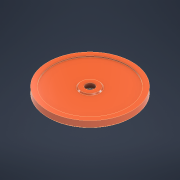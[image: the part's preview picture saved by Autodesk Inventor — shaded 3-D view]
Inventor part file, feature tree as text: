
AUTODESK INVENTOR PART (.ipt)
format: ipt  version: 2022 (Build 260153000, 153)  size: 141,824 bytes
history: native  units: mm
features: chamfer x2, revolve x1, sketch x1
ambient origin geometry x8: Origin, YZ Plane, XZ Plane, XY Plane, X Axis, Y Axis, Z Axis, Center Point
bodies: Solid1 (feature_tree)
feature tree (4):
  revolve  "Revolution1"  [1 undecoded]
  chamfer  "Chamfer1"  Angle=360.0deg  [1 undecoded]
  chamfer  "Chamfer2"  Distance=1.0mm
  sketch  "Sketch1"  dims[d0=8.0mm d3=16.0mm d7=360.0deg d8=1.0mm d9=1.0mm d10=4.0mm d11=78.0mm d12=1.0mm d13=2.0mm d14=45.0deg d15=0.5mm d16=2.0mm d17=45.0deg d18=69.0mm d23=0.25mm d24=2.0mm]
note: 2 required parameter values undecoded (feature->parameter linkage not recoverable at this tier; creation-order binding heuristic only, values carry confidence <= 0.55)